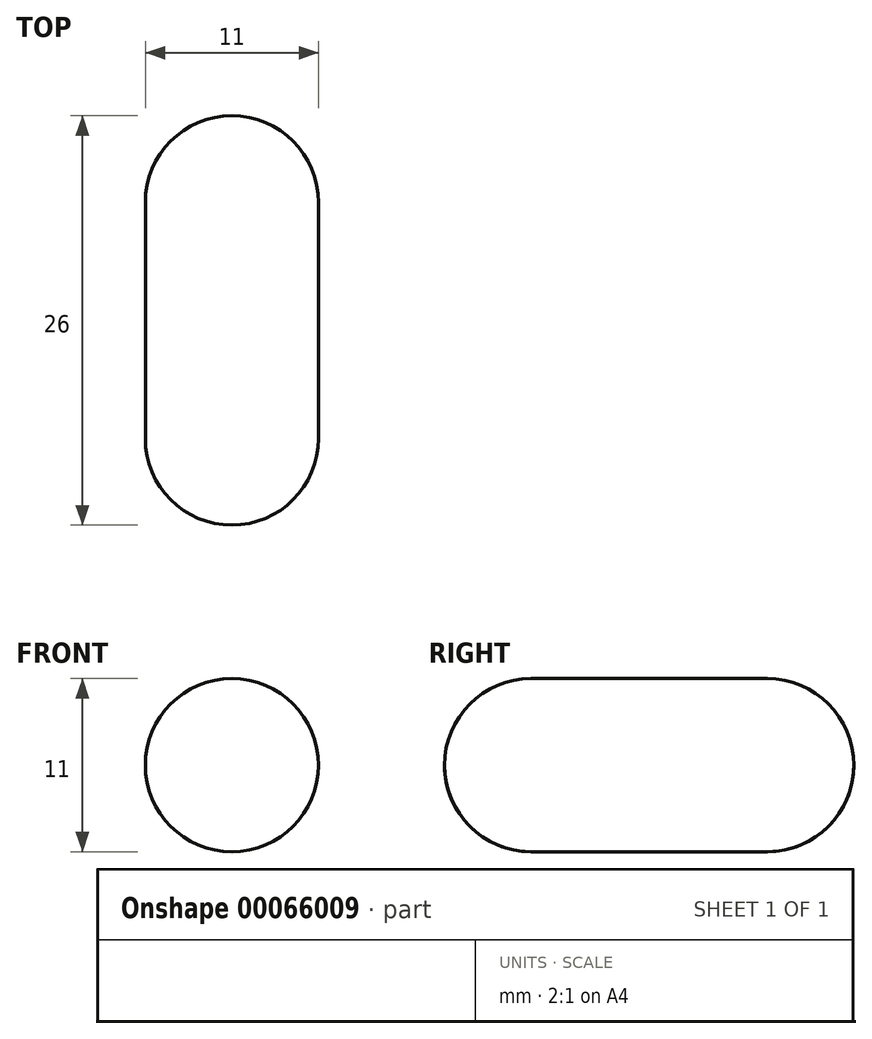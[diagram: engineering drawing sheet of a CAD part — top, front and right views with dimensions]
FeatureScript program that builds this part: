
annotation { "Feature Type Name" : "Feature", "Feature Type Description" : "" }
export const myFeature = defineFeature(function(context is Context, id is Id, definition is map)
    precondition{}
    {
        {
            var Q0;
            Q0=qCreatedBy(makeId("Right.planeOp"),FACE);
            var sketch = newSketch(context, id + "F0", { "sketchPlane" : qUnion([Q0])});
            skLineSegment(sketch, "E0.bottom", {"start": v(0, 0) * mm, "end": v(13, 0) * mm});
            skLineSegment(sketch, "E0.top", {"start": v(0, 5.5) * mm, "end": v(7.5, 5.5) * mm});
            skLineSegment(sketch, "E0.left", {"start": v(0, 0) * mm, "end": v(0, 5.5) * mm});
            skLineSegment(sketch, "E0.right", {"start": v(13, 0) * mm, "end": v(13, 0) * mm});
            skPoint(sketch, "E1.visualSharp", {"position": v(13, 5.5) * mm});
            skArc(sketch, "E1.filletArc", {"start": v(13, 0) * mm, "mid": v(11.39, 3.89) * mm, "end": v(7.5, 5.5) * mm});
            skSolve(sketch);
        }
        {
            var Q0;
            Q0 = qSketchRegion(id + "F0", true);
            var Q1;
            Q1=sQuery(id+"F0.wireOp",EDGE,"E0.bottom");
            revolve(context, id + "F1", {"entities" : qUnion([Q0]), "axis" : qUnion([Q1]), "revolveType" : RevolveType.FULL});
        }
        {
            var Q0;
            Q0=makeQuery(id+"F1.opRevolve","SWEPT_BODY",BODY,{"disambiguationData":[OSD([sQuery(id+"F0.wireOp",EDGE,"E0.bottom"),sQuery(id+"F0.wireOp",EDGE,"E0.top"),sQuery(id+"F0.wireOp",EDGE,"E0.left"),sQuery(id+"F0.wireOp",EDGE,"E1.filletArc")])]});
            var Q1;
            Q1=qCreatedBy(makeId("Front.planeOp"),FACE);
            mirror(context, id + "F2", {"operationType" : NewBodyOperationType.ADD, "entities" : qUnion([Q0]), "mirrorPlane" : qUnion([Q1])});
        }
    });
